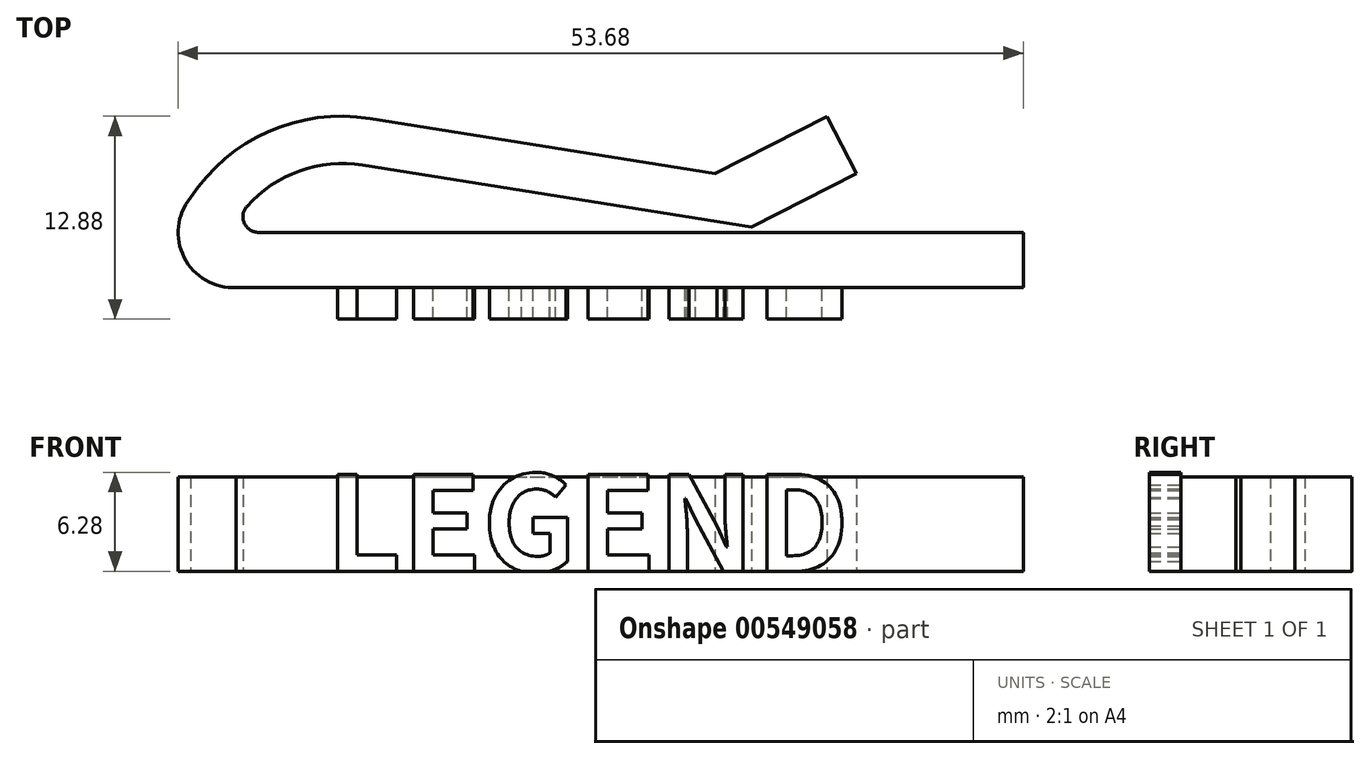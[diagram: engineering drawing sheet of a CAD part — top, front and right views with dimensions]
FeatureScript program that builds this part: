
annotation { "Feature Type Name" : "Feature", "Feature Type Description" : "" }
export const myFeature = defineFeature(function(context is Context, id is Id, definition is map)
    precondition{}
    {
        {
            var Q0;
            Q0=qCreatedBy(makeId("Top.planeOp"),FACE);
            var sketch = newSketch(context, id + "F0", { "sketchPlane" : qUnion([Q0])});
            skLineSegment(sketch, "E0.bottom", {"start": v(1.43, 0) * mm, "end": v(50, 0) * mm});
            skLineSegment(sketch, "E0.top", {"start": v(0, -3.5) * mm, "end": v(50, -3.5) * mm});
            skLineSegment(sketch, "E0.right", {"start": v(50, 0) * mm, "end": v(50, -3.5) * mm});
            skArc(sketch, "E1", {"start": v(8.5, 7.23) * mm, "mid": v(2.06, 6.4) * mm, "end": v(-2.9, 2.2) * mm});
            skArc(sketch, "E2", {"start": v(8.04, 4.27) * mm, "mid": v(4.03, 3.9) * mm, "end": v(0.69, 1.66) * mm});
            skPoint(sketch, "E0.left.start.orphan", {"position": v(0, 0) * mm});
            skArc(sketch, "E3.trimOffspring", {"start": v(-2.9, 2.2) * mm, "mid": v(-3.3, -1.6) * mm, "end": v(0, -3.5) * mm});
            skArc(sketch, "E4", {"start": v(0.69, 1.66) * mm, "mid": v(0.52, 0.59) * mm, "end": v(1.43, 0) * mm});
            skLineSegment(sketch, "E5", {"start": v(8.04, 4.27) * mm, "end": v(32.74, 0.33) * mm});
            skLineSegment(sketch, "E6", {"start": v(8.5, 7.23) * mm, "end": v(30.43, 3.73) * mm});
            skLineSegment(sketch, "E7", {"start": v(30.43, 3.73) * mm, "end": v(37.54, 7.37) * mm});
            skLineSegment(sketch, "E8", {"start": v(37.54, 7.37) * mm, "end": v(39.4, 3.73) * mm});
            skLineSegment(sketch, "E9", {"start": v(39.4, 3.73) * mm, "end": v(32.74, 0.33) * mm});
            skSolve(sketch);
        }
        {
            var Q0;
            Q0 = qSketchRegion(id + "F0", true);
            extrude(context, id + "F1", {"entities" : qUnion([Q0]), "depth" : 6 * mm, "offsetDistance" : 25 * mm});
        }
        {
            var Q0;
            Q0=makeQuery(id+"F1.opExtrude","SWEPT_FACE",FACE,{"disambiguationData":[OSD([sQuery(id+"F0.wireOp",EDGE,"E0.top")])]});
            var sketch = newSketch(context, id + "F2", { "sketchPlane" : qUnion([Q0])});
            skText(sketch, "E10", { "text": "LEGEND", "fontName": "NotoSansCJKsc-Bold.otf"});
            const initialGuessF2  = {"E10": [0.0057, 0, 1, 0, 0.006]};
            skSetInitialGuess(sketch, initialGuessF2);
            skSolve(sketch);
        }
        {
            var Q0;
            Q0 = qSketchRegion(id + "F2", true);
            extrude(context, id + "F3", {"entities" : qUnion([Q0]), "operationType" : NewBodyOperationType.ADD, "depth" : 2 * mm, "offsetDistance" : 25 * mm});
        }
        {
            var Q0;
            {var subQ12=sQuery(id+"F0.wireOp",EDGE,"E0.right");var subQ13=sQuery(id+"F0.wireOp",EDGE,"E0.top");Q0=makeQuery(id+"F3.boolean.opBoolean","SPLIT",FACE,{"disambiguationData":[TD([makeQuery(id+"F1.opExtrude","SWEPT_FACE",FACE,{"disambiguationData":[OSD([subQ12])]})])],"derivedFrom":makeQuery(id+"F1.opExtrude","SWEPT_FACE",FACE,{"disambiguationData":[OSD([subQ13])]})});}
            var sketch = newSketch(context, id + "F4", { "sketchPlane" : qUnion([Q0])});
            skLineSegment(sketch, "E11.bottom", {"start": v(0, 0) * mm, "end": v(50, 0) * mm});
            skLineSegment(sketch, "E11.top", {"start": v(0, -8.57) * mm, "end": v(50, -8.57) * mm});
            skLineSegment(sketch, "E11.left", {"start": v(0, 0) * mm, "end": v(0, -8.57) * mm});
            skLineSegment(sketch, "E11.right", {"start": v(50, 0) * mm, "end": v(50, -8.57) * mm});
            skSolve(sketch);
        }
        {
            var Q0;
            Q0=makeQuery(id+"F4.imprint","IMPRINT",FACE,{"disambiguationData":[TD([[makeQuery(id+"F4.imprint","IMPRINT",EDGE,{"derivedFrom":sQuery(id+"F4.wireOp",EDGE,"E11.top")}),1.0]])]});
            extrude(context, id + "F5", {"entities" : qUnion([Q0]), "operationType" : NewBodyOperationType.REMOVE, "depth" : 25 * mm, "offsetDistance" : 25 * mm});
        }
    });
